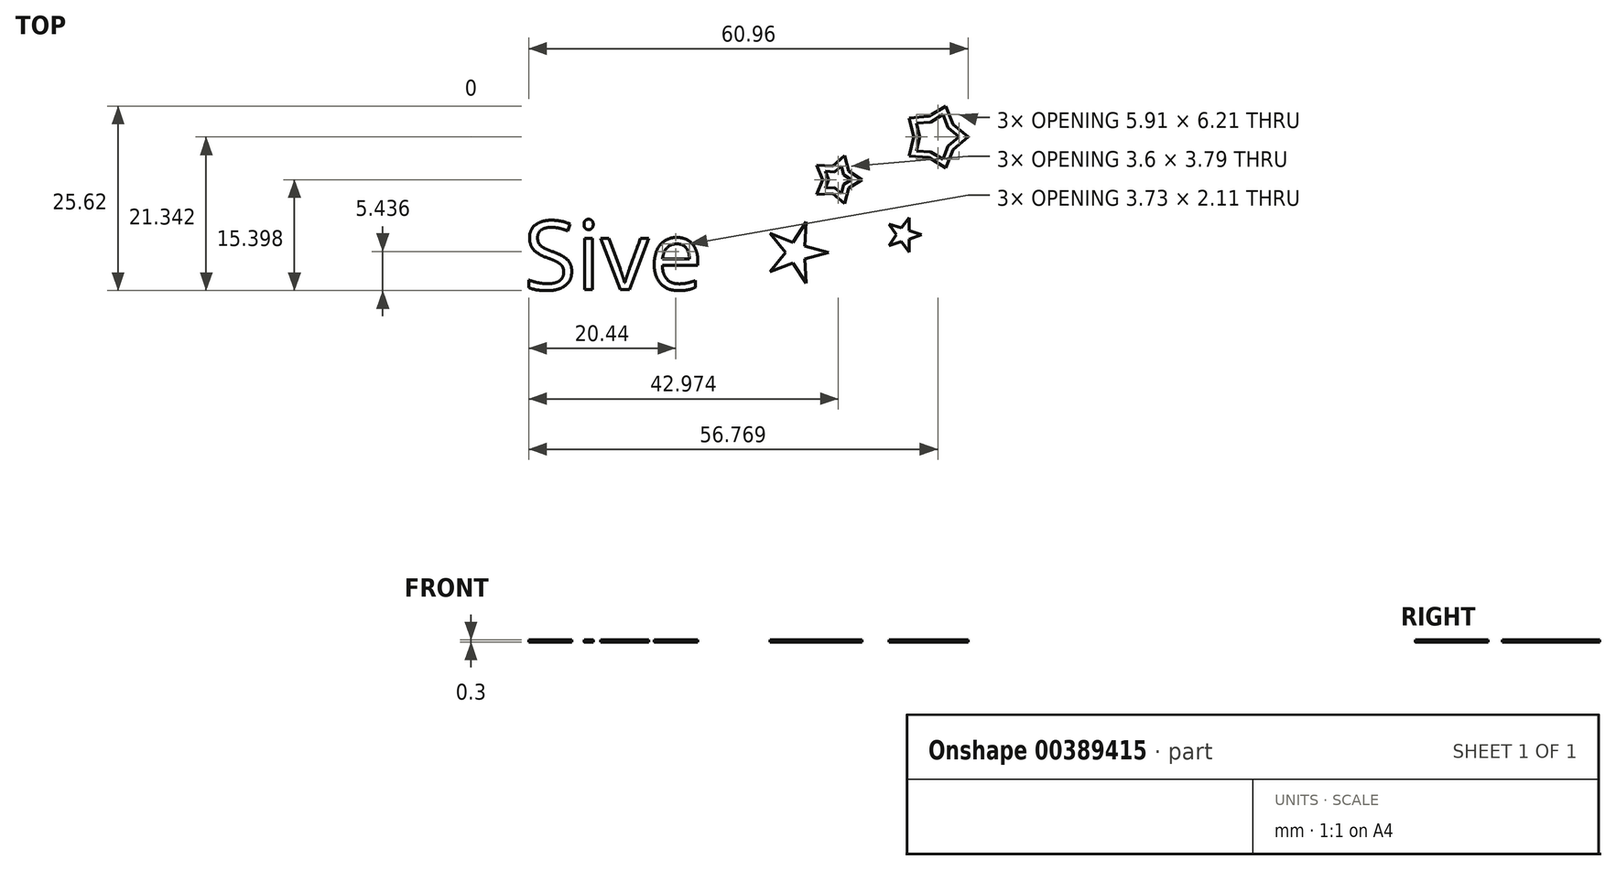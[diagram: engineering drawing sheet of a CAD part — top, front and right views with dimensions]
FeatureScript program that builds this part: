
annotation { "Feature Type Name" : "Feature", "Feature Type Description" : "" }
export const myFeature = defineFeature(function(context is Context, id is Id, definition is map)
    precondition{}
    {
        {
            var Q0;
            Q0=qCreatedBy(makeId("Top.planeOp"),FACE);
            var sketch = newSketch(context, id + "F0", { "sketchPlane" : qUnion([Q0])});
            skCircle(sketch, "E0.cCircle", {"center": v(46.45, 16.36) * mm, "radius": 4.5 * mm, "construction": true});
            skLineSegment(sketch, "E0.0", {"start": v(50.95, 16.36) * mm, "end": v(47.84, 12.08) * mm, "construction": true});
            skLineSegment(sketch, "E0.1", {"start": v(47.84, 12.08) * mm, "end": v(42.8, 13.72) * mm, "construction": true});
            skLineSegment(sketch, "E0.2", {"start": v(42.8, 13.72) * mm, "end": v(42.8, 19) * mm, "construction": true});
            skLineSegment(sketch, "E0.3", {"start": v(42.8, 19) * mm, "end": v(47.84, 20.64) * mm, "construction": true});
            skLineSegment(sketch, "E0.4", {"start": v(47.84, 20.64) * mm, "end": v(50.95, 16.36) * mm, "construction": true});
            skCircle(sketch, "E1.cCircle", {"center": v(46.45, 16.36) * mm, "radius": 3 * mm, "construction": true});
            skLineSegment(sketch, "E1.0", {"start": v(48.87, 18.13) * mm, "end": v(48.87, 14.6) * mm, "construction": true});
            skLineSegment(sketch, "E1.1", {"start": v(48.87, 14.6) * mm, "end": v(45.52, 13.5) * mm, "construction": true});
            skLineSegment(sketch, "E1.2", {"start": v(45.52, 13.5) * mm, "end": v(43.45, 16.36) * mm, "construction": true});
            skLineSegment(sketch, "E1.3", {"start": v(43.45, 16.36) * mm, "end": v(45.52, 19.21) * mm, "construction": true});
            skLineSegment(sketch, "E1.4", {"start": v(45.52, 19.21) * mm, "end": v(48.87, 18.13) * mm, "construction": true});
            skLineSegment(sketch, "E2", {"start": v(42.8, 19) * mm, "end": v(43.45, 16.36) * mm});
            skLineSegment(sketch, "E3", {"start": v(42.8, 13.72) * mm, "end": v(43.45, 16.36) * mm});
            skLineSegment(sketch, "E4", {"start": v(42.8, 13.72) * mm, "end": v(45.52, 13.5) * mm});
            skLineSegment(sketch, "E5", {"start": v(45.52, 13.5) * mm, "end": v(47.84, 12.08) * mm});
            skLineSegment(sketch, "E6", {"start": v(47.84, 12.08) * mm, "end": v(48.87, 14.6) * mm});
            skLineSegment(sketch, "E7", {"start": v(48.87, 14.6) * mm, "end": v(50.95, 16.36) * mm});
            skLineSegment(sketch, "E8", {"start": v(50.95, 16.36) * mm, "end": v(48.87, 18.13) * mm});
            skLineSegment(sketch, "E9", {"start": v(48.87, 18.13) * mm, "end": v(47.84, 20.64) * mm});
            skLineSegment(sketch, "E10", {"start": v(47.84, 20.64) * mm, "end": v(45.52, 19.21) * mm});
            skLineSegment(sketch, "E11", {"start": v(45.52, 19.21) * mm, "end": v(42.8, 19) * mm});
            skCircle(sketch, "E12.cCircle", {"center": v(32.77, 10.42) * mm, "radius": 3.5 * mm, "construction": true});
            skLineSegment(sketch, "E12.0", {"start": v(36.27, 10.42) * mm, "end": v(33.86, 7.09) * mm, "construction": true});
            skLineSegment(sketch, "E12.1", {"start": v(33.86, 7.09) * mm, "end": v(29.94, 8.36) * mm, "construction": true});
            skLineSegment(sketch, "E12.2", {"start": v(29.94, 8.36) * mm, "end": v(29.94, 12.47) * mm, "construction": true});
            skLineSegment(sketch, "E12.3", {"start": v(29.94, 12.47) * mm, "end": v(33.86, 13.75) * mm, "construction": true});
            skLineSegment(sketch, "E12.4", {"start": v(33.86, 13.75) * mm, "end": v(36.27, 10.42) * mm, "construction": true});
            skCircle(sketch, "E13.cCircle", {"center": v(32.77, 10.42) * mm, "radius": 2 * mm, "construction": true});
            skLineSegment(sketch, "E13.0", {"start": v(34.4, 11.6) * mm, "end": v(34.4, 9.24) * mm, "construction": true});
            skLineSegment(sketch, "E13.1", {"start": v(34.4, 9.24) * mm, "end": v(32.16, 8.52) * mm, "construction": true});
            skLineSegment(sketch, "E13.2", {"start": v(32.16, 8.52) * mm, "end": v(30.77, 10.42) * mm, "construction": true});
            skLineSegment(sketch, "E13.3", {"start": v(30.77, 10.42) * mm, "end": v(32.16, 12.32) * mm, "construction": true});
            skLineSegment(sketch, "E13.4", {"start": v(32.16, 12.32) * mm, "end": v(34.4, 11.6) * mm, "construction": true});
            skLineSegment(sketch, "E14", {"start": v(29.94, 12.47) * mm, "end": v(30.77, 10.42) * mm});
            skLineSegment(sketch, "E15", {"start": v(29.94, 8.36) * mm, "end": v(30.77, 10.42) * mm});
            skLineSegment(sketch, "E16", {"start": v(29.94, 8.36) * mm, "end": v(32.16, 8.52) * mm});
            skLineSegment(sketch, "E17", {"start": v(32.16, 8.52) * mm, "end": v(33.86, 7.09) * mm});
            skLineSegment(sketch, "E18", {"start": v(33.86, 7.09) * mm, "end": v(34.4, 9.24) * mm});
            skLineSegment(sketch, "E19", {"start": v(34.4, 9.24) * mm, "end": v(36.27, 10.42) * mm});
            skLineSegment(sketch, "E20", {"start": v(36.27, 10.42) * mm, "end": v(34.4, 11.6) * mm});
            skLineSegment(sketch, "E21", {"start": v(34.4, 11.6) * mm, "end": v(33.86, 13.75) * mm});
            skLineSegment(sketch, "E22", {"start": v(33.86, 13.75) * mm, "end": v(32.16, 12.32) * mm});
            skLineSegment(sketch, "E23", {"start": v(32.16, 12.32) * mm, "end": v(29.94, 12.47) * mm});
            skCircle(sketch, "E24.cCircle", {"center": v(41.99, 2.77) * mm, "radius": 2.5 * mm, "construction": true});
            skLineSegment(sketch, "E24.0", {"start": v(44.49, 2.77) * mm, "end": v(42.76, 0.39) * mm, "construction": true});
            skLineSegment(sketch, "E24.1", {"start": v(42.76, 0.39) * mm, "end": v(39.97, 1.3) * mm, "construction": true});
            skLineSegment(sketch, "E24.2", {"start": v(39.97, 1.3) * mm, "end": v(39.97, 4.24) * mm, "construction": true});
            skLineSegment(sketch, "E24.3", {"start": v(39.97, 4.24) * mm, "end": v(42.76, 5.14) * mm, "construction": true});
            skLineSegment(sketch, "E24.4", {"start": v(42.76, 5.14) * mm, "end": v(44.49, 2.77) * mm, "construction": true});
            skCircle(sketch, "E25.cCircle", {"center": v(41.99, 2.77) * mm, "radius": 1 * mm, "construction": true});
            skLineSegment(sketch, "E25.0", {"start": v(42.8, 3.36) * mm, "end": v(42.8, 2.18) * mm, "construction": true});
            skLineSegment(sketch, "E25.1", {"start": v(42.8, 2.18) * mm, "end": v(41.68, 1.82) * mm, "construction": true});
            skLineSegment(sketch, "E25.2", {"start": v(41.68, 1.82) * mm, "end": v(40.99, 2.77) * mm, "construction": true});
            skLineSegment(sketch, "E25.3", {"start": v(40.99, 2.77) * mm, "end": v(41.68, 3.72) * mm, "construction": true});
            skLineSegment(sketch, "E25.4", {"start": v(41.68, 3.72) * mm, "end": v(42.8, 3.36) * mm, "construction": true});
            skLineSegment(sketch, "E26", {"start": v(39.97, 4.24) * mm, "end": v(40.99, 2.77) * mm});
            skLineSegment(sketch, "E27", {"start": v(39.97, 1.3) * mm, "end": v(40.99, 2.77) * mm});
            skLineSegment(sketch, "E28", {"start": v(39.97, 1.3) * mm, "end": v(41.68, 1.82) * mm});
            skLineSegment(sketch, "E29", {"start": v(41.68, 1.82) * mm, "end": v(42.76, 0.39) * mm});
            skLineSegment(sketch, "E30", {"start": v(42.76, 0.39) * mm, "end": v(42.8, 2.18) * mm});
            skLineSegment(sketch, "E31", {"start": v(42.8, 2.18) * mm, "end": v(44.49, 2.77) * mm});
            skLineSegment(sketch, "E32", {"start": v(44.49, 2.77) * mm, "end": v(42.8, 3.36) * mm});
            skLineSegment(sketch, "E33", {"start": v(42.8, 3.36) * mm, "end": v(42.76, 5.14) * mm});
            skLineSegment(sketch, "E34", {"start": v(42.76, 5.14) * mm, "end": v(41.68, 3.72) * mm});
            skLineSegment(sketch, "E35", {"start": v(41.68, 3.72) * mm, "end": v(39.97, 4.24) * mm});
            skCircle(sketch, "E36.cCircle", {"center": v(27.11, 0.31) * mm, "radius": 4.5 * mm, "construction": true});
            skLineSegment(sketch, "E36.0", {"start": v(31.61, 0.31) * mm, "end": v(28.5, -3.97) * mm, "construction": true});
            skLineSegment(sketch, "E36.1", {"start": v(28.5, -3.97) * mm, "end": v(23.47, -2.33) * mm, "construction": true});
            skLineSegment(sketch, "E36.2", {"start": v(23.47, -2.33) * mm, "end": v(23.47, 2.96) * mm, "construction": true});
            skLineSegment(sketch, "E36.3", {"start": v(23.47, 2.96) * mm, "end": v(28.5, 4.6) * mm, "construction": true});
            skLineSegment(sketch, "E36.4", {"start": v(28.5, 4.6) * mm, "end": v(31.61, 0.31) * mm, "construction": true});
            skCircle(sketch, "E37.cCircle", {"center": v(27.11, 0.31) * mm, "radius": 1.5 * mm, "construction": true});
            skLineSegment(sketch, "E37.0", {"start": v(28.32, 1.2) * mm, "end": v(28.32, -0.57) * mm, "construction": true});
            skLineSegment(sketch, "E37.1", {"start": v(28.32, -0.57) * mm, "end": v(26.65, -1.11) * mm, "construction": true});
            skLineSegment(sketch, "E37.2", {"start": v(26.65, -1.11) * mm, "end": v(25.61, 0.31) * mm, "construction": true});
            skLineSegment(sketch, "E37.3", {"start": v(25.61, 0.31) * mm, "end": v(26.65, 1.74) * mm, "construction": true});
            skLineSegment(sketch, "E37.4", {"start": v(26.65, 1.74) * mm, "end": v(28.32, 1.2) * mm, "construction": true});
            skLineSegment(sketch, "E38", {"start": v(23.47, 2.96) * mm, "end": v(25.61, 0.31) * mm});
            skLineSegment(sketch, "E39", {"start": v(23.47, -2.33) * mm, "end": v(25.61, 0.31) * mm});
            skLineSegment(sketch, "E40", {"start": v(23.47, -2.33) * mm, "end": v(26.65, -1.11) * mm});
            skLineSegment(sketch, "E41", {"start": v(26.65, -1.11) * mm, "end": v(28.5, -3.97) * mm});
            skLineSegment(sketch, "E42", {"start": v(28.5, -3.97) * mm, "end": v(28.32, -0.57) * mm});
            skLineSegment(sketch, "E43", {"start": v(28.32, -0.57) * mm, "end": v(31.61, 0.31) * mm});
            skLineSegment(sketch, "E44", {"start": v(31.61, 0.31) * mm, "end": v(28.32, 1.2) * mm});
            skLineSegment(sketch, "E45", {"start": v(28.32, 1.2) * mm, "end": v(28.5, 4.6) * mm});
            skLineSegment(sketch, "E46", {"start": v(28.5, 4.6) * mm, "end": v(26.65, 1.74) * mm});
            skLineSegment(sketch, "E47", {"start": v(26.65, 1.74) * mm, "end": v(23.47, 2.96) * mm});
            skLineSegment(sketch, "E48.0", {"start": v(48.2, 17.64) * mm, "end": v(47.46, 19.47) * mm});
            skLineSegment(sketch, "E48.1", {"start": v(49.71, 16.36) * mm, "end": v(48.2, 17.64) * mm});
            skLineSegment(sketch, "E48.2", {"start": v(47.46, 19.47) * mm, "end": v(45.77, 18.43) * mm});
            skLineSegment(sketch, "E48.3", {"start": v(48.2, 15.08) * mm, "end": v(49.71, 16.36) * mm});
            skLineSegment(sketch, "E48.4", {"start": v(47.46, 13.26) * mm, "end": v(48.2, 15.08) * mm});
            skLineSegment(sketch, "E48.5", {"start": v(45.77, 14.3) * mm, "end": v(47.46, 13.26) * mm});
            skLineSegment(sketch, "E48.6", {"start": v(45.77, 18.43) * mm, "end": v(43.8, 18.28) * mm});
            skLineSegment(sketch, "E48.7", {"start": v(43.8, 18.28) * mm, "end": v(44.27, 16.36) * mm});
            skLineSegment(sketch, "E48.8", {"start": v(43.8, 14.44) * mm, "end": v(44.27, 16.36) * mm});
            skLineSegment(sketch, "E48.9", {"start": v(43.8, 14.44) * mm, "end": v(45.77, 14.3) * mm});
            skLineSegment(sketch, "E49.0", {"start": v(33.7, 11.09) * mm, "end": v(33.39, 12.31) * mm});
            skLineSegment(sketch, "E49.1", {"start": v(34.76, 10.42) * mm, "end": v(33.7, 11.09) * mm});
            skLineSegment(sketch, "E49.2", {"start": v(33.39, 12.31) * mm, "end": v(32.42, 11.5) * mm});
            skLineSegment(sketch, "E49.3", {"start": v(33.7, 9.75) * mm, "end": v(34.76, 10.42) * mm});
            skLineSegment(sketch, "E49.4", {"start": v(33.39, 8.53) * mm, "end": v(33.7, 9.75) * mm});
            skLineSegment(sketch, "E49.5", {"start": v(32.42, 9.34) * mm, "end": v(33.39, 8.53) * mm});
            skLineSegment(sketch, "E49.6", {"start": v(32.42, 11.5) * mm, "end": v(31.16, 11.59) * mm});
            skLineSegment(sketch, "E49.7", {"start": v(31.16, 11.59) * mm, "end": v(31.64, 10.42) * mm});
            skLineSegment(sketch, "E49.8", {"start": v(31.16, 9.25) * mm, "end": v(31.64, 10.42) * mm});
            skLineSegment(sketch, "E49.9", {"start": v(31.16, 9.25) * mm, "end": v(32.42, 9.34) * mm});
            skText(sketch, "E50", { "text": "Sive", "fontName": "OpenSans-Regular.ttf"});
            const initialGuessF0  = {"E50": [-0.0107, -0.00485, 1, 0, 0.0096]};
            skSetInitialGuess(sketch, initialGuessF0);
            skSolve(sketch);
        }
        {
            var Q0;
            Q0=qSketchRegion(id+"F0",true);
            extrude(context, id + "F1", {"entities" : qUnion([Q0]), "depth" : 0.3 * mm});
        }
    });
